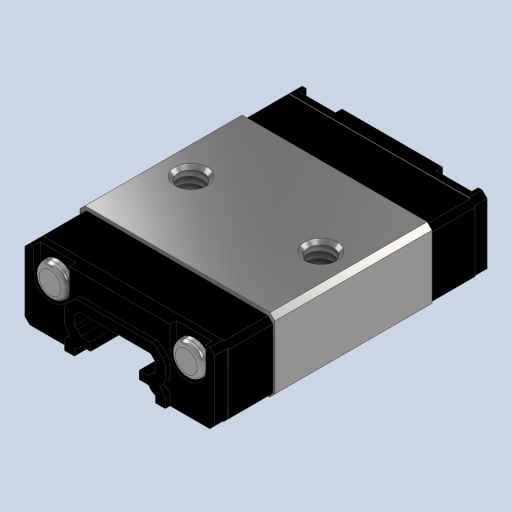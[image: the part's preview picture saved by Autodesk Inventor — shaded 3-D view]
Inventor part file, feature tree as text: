
AUTODESK INVENTOR PART (.ipt)
format: ipt  version: 2023 (Build 270158000, 158)  size: 640,000 bytes
history: native  units: mm
features: sketch x21, extrude x18, other x7, revolve x4, hole x1, pattern_linear x1
ambient origin geometry x8: Origin, YZ Plane, XZ Plane, XY Plane, X Axis, Y Axis, Z Axis, Center Point
bodies: Solid1 (feature_tree)
feature tree (52):
  extrude  "Extrusion1"  Depth=3.85mm TaperAngle=0.0deg
  extrude  "Extrusion2"  Depth=3.85mm TaperAngle=0.0deg
  extrude  "Extrusion3"  Depth=1.1mm TaperAngle=0.0deg
  extrude  "Extrusion4"  Depth=1.1mm TaperAngle=0.0deg
  extrude  "Extrusion5"  Depth=0.4mm TaperAngle=0.0deg
  extrude  "Extrusion6"  Depth=0.4mm TaperAngle=0.0deg
  extrude  "Extrusion7"  TaperAngle=360.0deg  [1 undecoded]
  extrude  "Extrusion8"  TaperAngle=360.0deg  [1 undecoded]
  extrude  "Extrusion9"  Depth=9.7mm TaperAngle=0.0deg
  extrude  "Extrusion10"  Depth=0.05mm TaperAngle=0.0deg
  extrude  "Extrusion11"  Depth=0.05mm TaperAngle=0.0deg
  extrude  "Extrusion12"  Depth=10.0mm TaperAngle=0.0deg
  extrude  "Extrusion13"  [1 undecoded]
  revolve  "Revolution1"  [1 undecoded]
  revolve  "Revolution2"  [1 undecoded]
  revolve  "Revolution3"  [1 undecoded]
  revolve  "Revolution4"  [1 undecoded]
  extrude  "Extrusion14"  [1 undecoded]
  extrude  "Extrusion15"  [1 undecoded]
  extrude  "Extrusion16"  [1 undecoded]
  extrude  "Extrusion17"  [1 undecoded]
  extrude  "Extrusion18"  [1 undecoded]
  hole  "Hole1"  [1 undecoded]
  pattern_linear  "Rectangular Pattern1"  [2 undecoded]
  other  "to_rail_XY"
  other  "to_rail_YZ"
  other  "to_rail_ZX"
  other  "to_rail_X"
  other  "to_rail_Y"
  other  "to_rail_Z"
  other  "to_rail_Center"
  sketch  "Sketch_29"  dims[d29=360.0deg d30=9.7mm d31=0.0mm]
  sketch  "Sketch_3"  dims[d0=9.7mm d1=0.0mm d2=3.85mm d3=0.0mm]
  sketch  "Sketch_42"
  sketch  "Sketch_4"  dims[d4=2.75mm d5=0.0mm d6=3.85mm d7=0.0mm]
  sketch  "Sketch_43"
  sketch  "Sketch_30"  dims[d32=4.85mm d33=0.0mm d34=0.05mm d35=0.0mm]
  sketch  "Sketch_31"  dims[d36=4.85mm d37=0.0mm d38=0.05mm d39=0.0mm]
  sketch  "Sketch_32"  dims[d40=1.567mm d41=1.5mm d42=2.0mm d43=2.0mm d44=90.0deg d45=2.3mm d46=120.0deg d47=20.0mm d49=8.0mm d50=10.0mm d52=0.0mm]
  sketch  "Sketch_33"
  sketch  "Sketch_34"
  sketch  "Sketch_35"
  sketch  "Sketch_36"
  sketch  "Sketch_37"
  sketch  "Sketch_38"
  sketch  "Sketch_39"
  sketch  "Sketch_17"  dims[d16=0.3mm d17=0.0mm d18=0.4mm d19=0.0mm]
  sketch  "Sketch_11"  dims[d12=0.3mm d13=0.0mm d14=1.1mm d15=0.0mm]
  sketch  "Sketch_22"  dims[d20=0.4mm d21=0.0mm d22=0.4mm d23=0.0mm]
  sketch  "Sketch_10"  dims[d8=2.75mm d9=0.0mm d10=1.1mm d11=0.0mm]
  sketch  "Sketch_23"  dims[d24=0.4mm d25=0.0mm d26=360.0deg]
  sketch  "Sketch23"  dims[d27=360.0deg d28=360.0deg]
note: 15 required parameter values undecoded (feature->parameter linkage not recoverable at this tier; creation-order binding heuristic only, values carry confidence <= 0.55)
